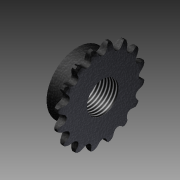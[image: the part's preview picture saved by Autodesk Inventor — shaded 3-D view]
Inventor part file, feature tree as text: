
AUTODESK INVENTOR PART (.ipt)
format: ipt  version: 2012 (Build 160160000, 160)  size: 965,632 bytes
history: native  units: in
note: dims shown in document units (in); Inventor stores cm internally (conversion verified against a paired STEP export)
features: imported_body x1, extrude x1, thread x1, sketch x1
ambient origin geometry x8: Origin, YZ Plane, XZ Plane, XY Plane, X Axis, Y Axis, Z Axis, Center Point
bodies: Solid1 (feature_tree)
feature tree (4):
  imported_body  "Base1"
  extrude  "Extrusion1"  Depth=1.0in TaperAngle=0.0deg
  thread  "Thread1"  [1 undecoded]
  sketch  "Sketch1"  dims[d0=0.5in d1=1.0in d2=0.0in d3=1.0in d4=0.0in]
note: 1 required parameter value undecoded (feature->parameter linkage not recoverable at this tier; creation-order binding heuristic only, values carry confidence <= 0.55)
